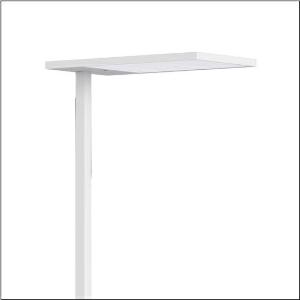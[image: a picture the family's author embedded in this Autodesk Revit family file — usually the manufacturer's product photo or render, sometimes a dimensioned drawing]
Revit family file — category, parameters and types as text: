
# Revit family: silica_r__21_floor_r_51mx53sg4dw_45fa
name_source: partatom
category: Lighting Fixtures
units: mm (PartAtom-declared; Revit-internal decimal feet)

## family parameters
Cut with Voids When Loaded = No
Host = Face
Light Source = No
Part Type = Normal
Room Calculation Point = No
Round Connector Dimension = Use Diameter
Shared = No

## types (1)
- Silica® 21 Floor R (1 x LED, 15000 lm, 106.4 W, 4000K)
    Apparent Load = 106 VA
    CIE Flux Codes = 54 86 97 13 100
    Color Rendering = 80
    Color Temperature = 4000K
    Default Elevation = 1800 mm
    Description = Silica® 21 Floor R, floorstanding luminaire, of PMMA, primary optical cover: prismatic diffuser, of PMMA, CAT 2 (L<= 3000cd/m²), light emission: indirect/direct distribution, primary light characteristic: symmetric, primary optical cover: cover panel, of PMMA, installation type: not mounted, LED, rated luminous flux: 15.000lm, luminous efficacy: 141lm/W, light colour: 840, colour temperature: 4000K, daylight-dependent control, mains connection: 230V, AC, 50/60Hz, connection cable pre-assembled, cable length: 2,5m, rated input power: 106.4W, luminaire head, of aluminium, coated, traffic white (RAL 9016), length: 671mm, width: 330mm, height: 2010mm, supporting column, angular, of aluminium, coated, traffic white (RAL 9016), baseplate, of steel, coated, traffic white (RAL 9016), protection rating (complete): IP20, insulation class (complete): insulation class I (protective earthing), certification: CE, standard: EN 50419, packaging unit: 1 piece
    Height = 18 mm
    Lamp = 1 x LED
    Lamp Light Flux = 15000 lm
    Lamp Power = 106.4 W
    Lamp count = 1
    Length = 650 mm
    Luminous efficacy = 141 lm/W
    Manufacturer = Siteco
    ModVariant = No
    Model = 51MX53SG4DW
    Mounting Place = Floor
    Mounting Type = Freestanding
    Number of Poles = 1
    OnlyDefault = Yes
    Power Factor = 1
    Product Name = Silica® 21 Floor R
    Product group = floorstanding luminaire
    ProductGroupID = 1302
    Protection Class = Protection class I
    Protection Degree = IP 20
    RLX_Detail_Level = 1
    RLX_Emergency_Light_Flux = 0 lm
    RLX_Emergency_Type = 0
    RLX_Emergency_Type_DB = No
    RlxData = <blob elided: 18621 chars, md5=841c51a3>
    Socket = socket
    Standby Power = 0 W
    System Light Flux = 15000 lm
    System Power = 106 W
    Type Comments = Product without accessories
    Type Image = l_1003935.jpg
    URL = http://relux.com
    VarID = ---
    Voltage = 0 V
    Weight = 0.00 kg
    Width = 350 mm

## geometry (parser evidence)
native form markers: Blend x4, Sweep x14
no freeform markers — native parametric forms only
